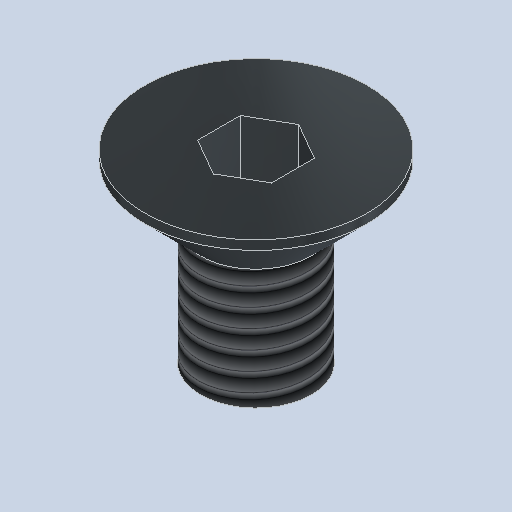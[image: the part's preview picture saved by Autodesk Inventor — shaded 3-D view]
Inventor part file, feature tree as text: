
AUTODESK INVENTOR PART (.ipt)
format: ipt  version: 2023 (Build 270158030, 158C)  size: 166,400 bytes
history: native  units: mm
features: extrude x3, sketch x3, other x1, thread x1, chamfer x1
ambient origin geometry x8: Origin, YZ Plane, XZ Plane, XY Plane, X Axis, Y Axis, Z Axis, Center Point
bodies: Body1 (feature_tree)
feature tree (9):
  other  "ソリッド1"
  extrude  "押し出し1"  Depth=3.0mm
  thread  "ねじ1"
  extrude  "押し出し2"  Depth=5.0mm TaperAngle=0.0deg
  chamfer  "面取り1"  Distance=10.0mm
  extrude  "押し出し3"  Depth=6.0mm
  sketch  "スケッチ1"
  sketch  "スケッチ2"
  sketch  "スケッチ3"
